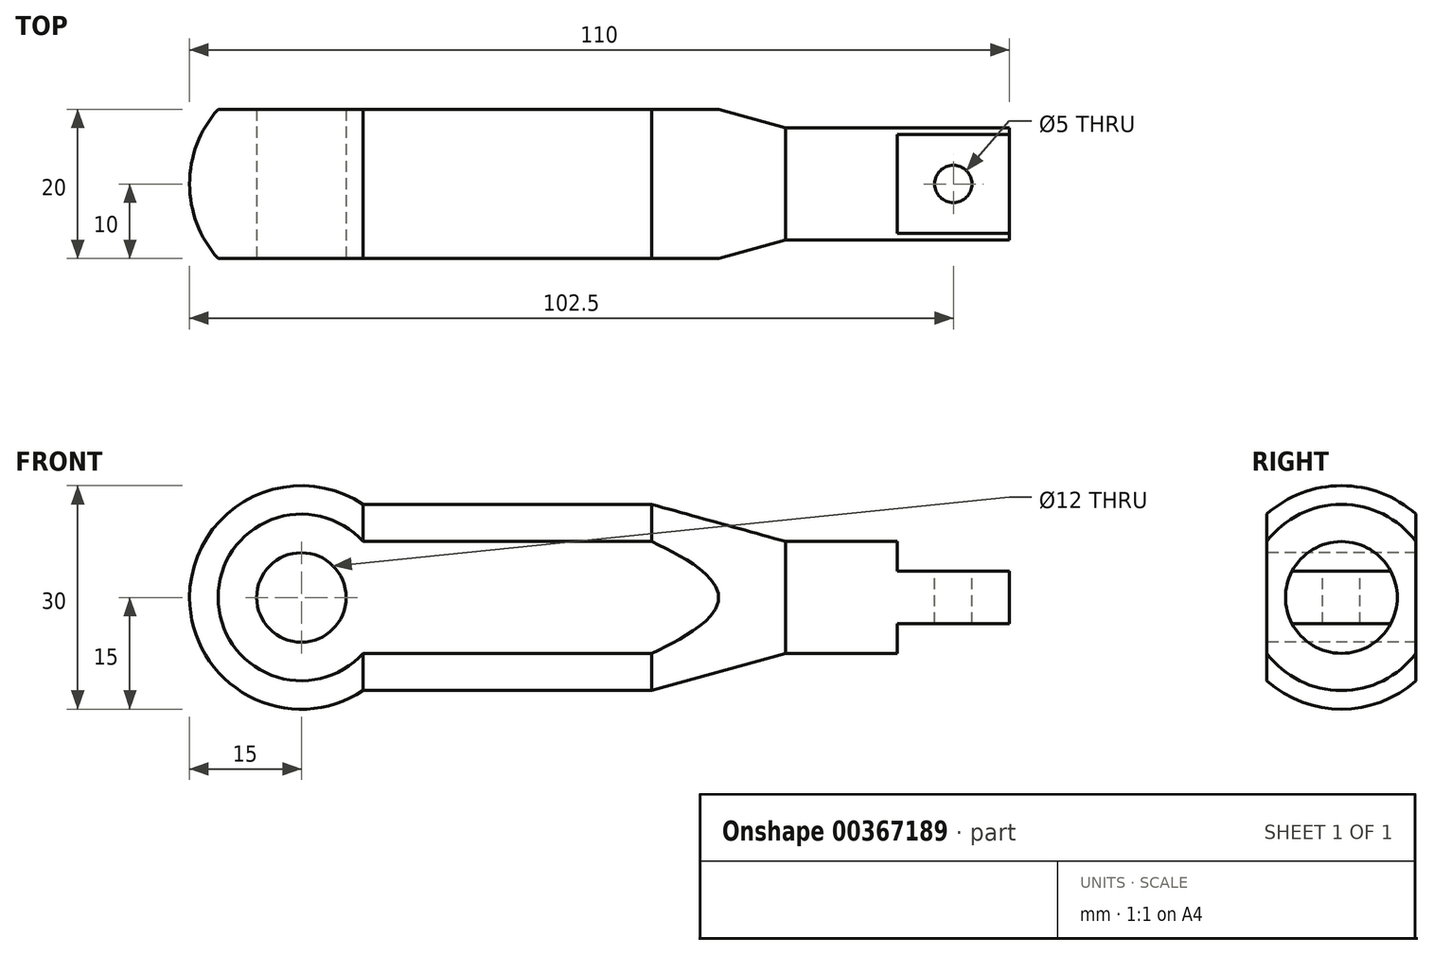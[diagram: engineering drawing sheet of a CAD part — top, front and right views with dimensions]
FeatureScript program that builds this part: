
annotation { "Feature Type Name" : "Feature", "Feature Type Description" : "" }
export const myFeature = defineFeature(function(context is Context, id is Id, definition is map)
    precondition{}
    {
        {
            var Q0;
            Q0=qCreatedBy(makeId("Front.planeOp"),FACE);
            var sketch = newSketch(context, id + "F0", { "sketchPlane" : qUnion([Q0])});
            skLineSegment(sketch, "E0", {"start": v(0, 0) * mm, "end": v(128.65, 0) * mm, "construction": true});
            skArc(sketch, "E1", {"start": v(-15, 0) * mm, "mid": v(-7.1, 13.22) * mm, "end": v(8.3, 12.5) * mm});
            skLineSegment(sketch, "E2", {"start": v(8.3, 12.5) * mm, "end": v(47, 12.5) * mm});
            skLineSegment(sketch, "E3", {"start": v(47, 12.5) * mm, "end": v(65, 7.5) * mm});
            skLineSegment(sketch, "E4", {"start": v(64.87, 7.5) * mm, "end": v(65, 7.5) * mm});
            skLineSegment(sketch, "E5", {"start": v(95, 0) * mm, "end": v(-15, 0) * mm});
            skLineSegment(sketch, "E6", {"start": v(65, 7.5) * mm, "end": v(95, 7.5) * mm});
            skLineSegment(sketch, "E7", {"start": v(95, 7.5) * mm, "end": v(95, 0) * mm});
            skSolve(sketch);
        }
        {
            var Q0;
            Q0=qSketchRegion(id+"F0",true);
            var Q1;
            Q1=sQuery(id+"F0.wireOp",EDGE,"E0");
            revolve(context, id + "F1", {"entities" : qUnion([Q0]), "axis" : qUnion([Q1]), "revolveType" : RevolveType.FULL});
        }
        {
            var Q0;
            Q0=qCreatedBy(makeId("Front.planeOp"),FACE);
            var sketch = newSketch(context, id + "F2", { "sketchPlane" : qUnion([Q0])});
            skLineSegment(sketch, "E8.bottom", {"start": v(95, 3.5) * mm, "end": v(80, 3.5) * mm});
            skLineSegment(sketch, "E8.right", {"start": v(80, 3.5) * mm, "end": v(80, 7.5) * mm});
            skLineSegment(sketch, "E9", {"start": v(80, 7.5) * mm, "end": v(95, 7.5) * mm});
            skLineSegment(sketch, "E10", {"start": v(95, 7.5) * mm, "end": v(95, 3.5) * mm});
            skLineSegment(sketch, "E11", {"start": v(75.4, 0) * mm, "end": v(108.09, 0) * mm, "construction": true});
            skLineSegment(sketch, "E12.MirrorCS", {"start": v(95, -7.5) * mm, "end": v(95, -3.5) * mm});
            skLineSegment(sketch, "E13.MirrorCS", {"start": v(80, -3.5) * mm, "end": v(80, -7.5) * mm});
            skLineSegment(sketch, "E14.MirrorCS", {"start": v(80, -7.5) * mm, "end": v(95, -7.5) * mm});
            skLineSegment(sketch, "E15.MirrorCS", {"start": v(95, -3.5) * mm, "end": v(80, -3.5) * mm});
            skSolve(sketch);
        }
        {
            var Q0;
            Q0=qSketchRegion(id+"F2",true);
            extrude(context, id + "F3", {"entities" : qUnion([Q0]), "operationType" : NewBodyOperationType.REMOVE, "endBound" : BoundingType.THROUGH_ALL, "depth" : 25 * mm, "hasSecondDirection" : true, "secondDirectionBound" : SecondDirectionBoundingType.THROUGH_ALL, "secondDirectionOppositeDirection" : true, "secondDirectionDepth" : 25 * mm});
        }
        {
            var Q0;
            Q0=makeQuery(id+"F1.opRevolve","SWEPT_FACE",FACE,{"disambiguationData":[OSD([sQuery(id+"F0.wireOp",EDGE,"E7")])]});
            var sketch = newSketch(context, id + "F4", { "sketchPlane" : qUnion([Q0])});
            skArc(sketch, "E16", {"start": v(-10, 11.18) * mm, "mid": v(-15, 0) * mm, "end": v(-10, -11.18) * mm});
            skLineSegment(sketch, "E17", {"start": v(-10, 11.18) * mm, "end": v(-10, -11.18) * mm});
            skLineSegment(sketch, "E18", {"start": v(10, 11.18) * mm, "end": v(10, -11.18) * mm});
            skLineSegment(sketch, "E19", {"start": v(0, 0) * mm, "end": v(0, 34.48) * mm, "construction": true});
            skArc(sketch, "E20.trimOffspring", {"start": v(10, -11.18) * mm, "mid": v(15, 0) * mm, "end": v(10, 11.18) * mm});
            skSolve(sketch);
        }
        {
            var Q0;
            Q0=qSketchRegion(id+"F4",true);
            extrude(context, id + "F5", {"entities" : qUnion([Q0]), "operationType" : NewBodyOperationType.REMOVE, "endBound" : BoundingType.THROUGH_ALL, "oppositeDirection" : true, "depth" : 25 * mm});
        }
        {
            var Q0;
            Q0=qCreatedBy(makeId("Front.planeOp"),FACE);
            var sketch = newSketch(context, id + "F6", { "sketchPlane" : qUnion([Q0])});
            skCircle(sketch, "E21", {"center": v(0, 0) * mm, "radius": 6 * mm});
            skSolve(sketch);
        }
        {
            var Q0;
            Q0=qSketchRegion(id+"F6",true);
            extrude(context, id + "F7", {"entities" : qUnion([Q0]), "operationType" : NewBodyOperationType.REMOVE, "endBound" : BoundingType.THROUGH_ALL, "oppositeDirection" : true, "depth" : 25 * mm, "hasSecondDirection" : true, "secondDirectionBound" : SecondDirectionBoundingType.THROUGH_ALL, "secondDirectionOppositeDirection" : false, "secondDirectionDepth" : 25 * mm});
        }
        {
            var Q0;
            Q0=makeQuery(id+"F3.boolean.opBoolean","COPY",FACE,{"derivedFrom":makeQuery(id+"F3.opExtrude","SWEPT_FACE",FACE,{"disambiguationData":[OSD([sQuery(id+"F2.wireOp",EDGE,"E8.bottom")])]})});
            var sketch = newSketch(context, id + "F8", { "sketchPlane" : qUnion([Q0])});
            skCircle(sketch, "E22", {"center": v(87.5, 0) * mm, "radius": 2.5 * mm});
            skSolve(sketch);
        }
        {
            var Q0;
            Q0=qSketchRegion(id+"F8",true);
            extrude(context, id + "F9", {"entities" : qUnion([Q0]), "operationType" : NewBodyOperationType.REMOVE, "endBound" : BoundingType.THROUGH_ALL, "oppositeDirection" : true, "depth" : 25 * mm, "hasSecondDirection" : true, "secondDirectionBound" : SecondDirectionBoundingType.THROUGH_ALL, "secondDirectionOppositeDirection" : false, "secondDirectionDepth" : 25 * mm});
        }
    });
